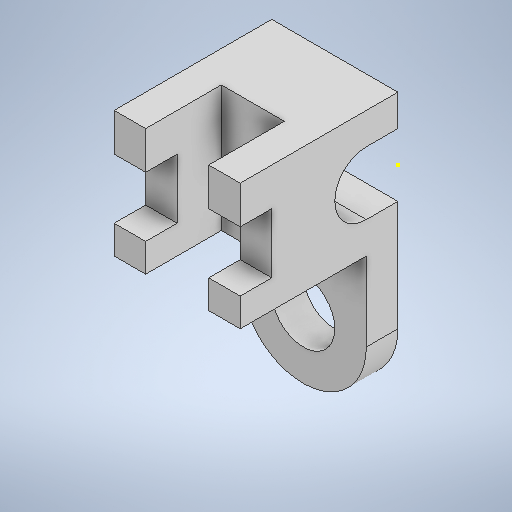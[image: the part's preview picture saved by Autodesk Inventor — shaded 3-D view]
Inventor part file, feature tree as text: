
AUTODESK INVENTOR PART (.ipt)
format: ipt  version: 2025.2 (Build 292293000, 293)  size: 606,208 bytes
history: native  units: in
note: dims shown in document units (in); Inventor stores cm internally (conversion verified against a paired STEP export)
features: sketch x9, extrude x6, rib x1, other x1
ambient origin geometry x8: Origin, YZ Plane, XZ Plane, XY Plane, X Axis, Y Axis, Z Axis, Center Point
bodies: Solid1 (feature_tree)
feature tree (17):
  extrude  "Extrusion1"  Depth=3.1496in
  extrude  "Extrusion2"  Depth=0.7874in
  sketch  "Sketch3"  dims[d14=1.4961in d16=3.937in d17=0.0in]
  extrude  "Extrusion3"  Depth=3.937in TaperAngle=0.0deg
  extrude  "Extrusion4"  Depth=0.7874in
  sketch  "Sketch6"  dims[d25=0.0in d26=0.0in d27=1.9685in]
  extrude  "Extrusion5"  Depth=0.7874in
  rib  "Rib1"
  extrude  "Extrusion6"  Depth=1.9685in
  sketch  "Sketch1"  dims[d9=3.1496in d10=3.1496in]
  other  "Image1"
  sketch  "Sketch2"  dims[d11=3.937in d12=0.0in d13=0.7874in]
  sketch  "Sketch4"  dims[d20=1.8898in d21=0.0in d22=0.7874in]
  sketch  "Sketch5"  dims[d23=1.5748in d24=0.7874in]
  sketch  "Sketch7"  dims[d28=1.5748in]
  sketch  "Sketch8"  dims[d29=3.1496in]
  sketch  "Sketch9"  dims[d31=0.7874in d32=0.0in d34=0.0394in d35=0.3937in d36=0.0in d37=0.0in d38=0.0394in d39=0.0394in d41=0.9449in d42=1.5748in d43=0.7874in d44=1.8898in d45=0.0in]
